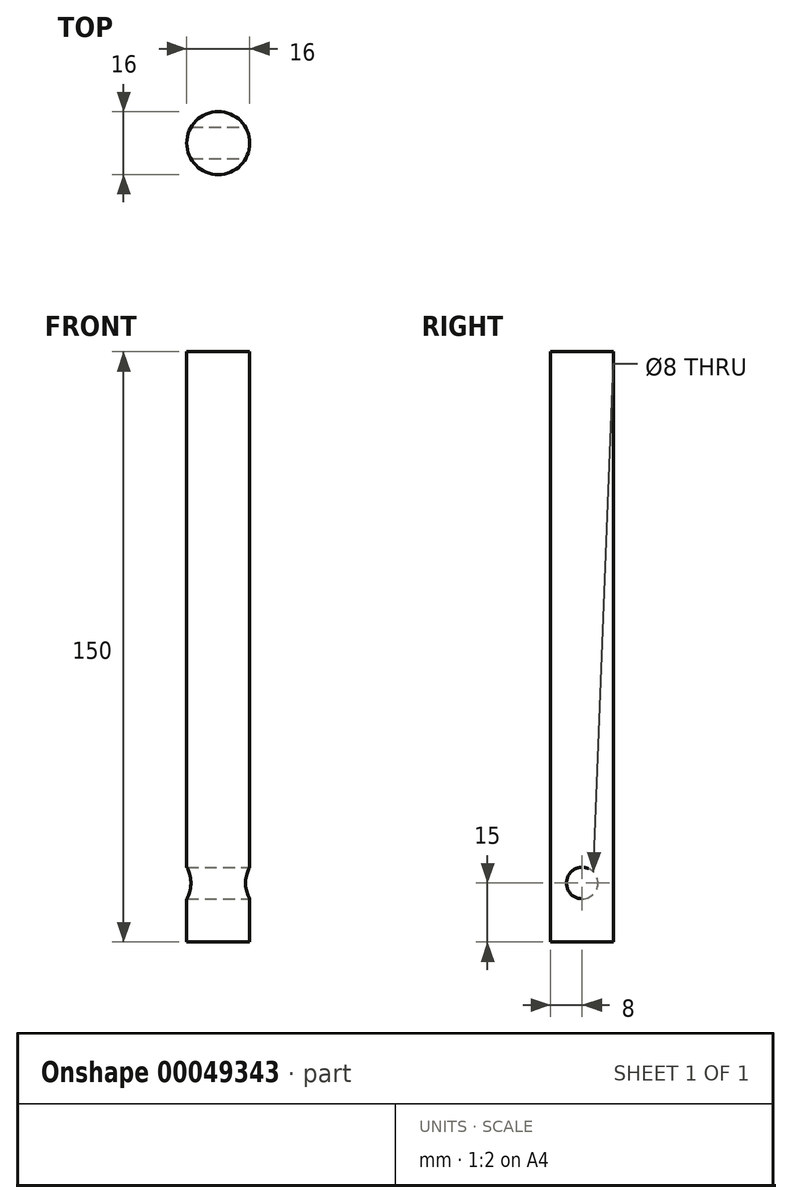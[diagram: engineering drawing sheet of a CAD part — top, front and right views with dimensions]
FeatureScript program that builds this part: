
annotation { "Feature Type Name" : "Feature", "Feature Type Description" : "" }
export const myFeature = defineFeature(function(context is Context, id is Id, definition is map)
    precondition{}
    {
        {
            var Q0;
            Q0=qCreatedBy(makeId("Top.planeOp"),FACE);
            var sketch = newSketch(context, id + "F0", { "sketchPlane" : qUnion([Q0])});
            skCircle(sketch, "E0", {"center": v(0, 0) * mm, "radius": 8 * mm});
            skSolve(sketch);
        }
        {
            var Q0;
            Q0=qSketchRegion(id+"F0",true);
            extrude(context, id + "F1", {"entities" : qUnion([Q0]), "depth" : 150 * mm});
        }
        {
            var Q0;
            Q0=qCreatedBy(makeId("Right.planeOp"),FACE);
            var sketch = newSketch(context, id + "F2", { "sketchPlane" : qUnion([Q0])});
            skCircle(sketch, "E1", {"center": v(0, 15) * mm, "radius": 4 * mm});
            skSolve(sketch);
        }
        {
            var Q0;
            Q0=qSketchRegion(id+"F2",true);
            extrude(context, id + "F3", {"entities" : qUnion([Q0]), "operationType" : NewBodyOperationType.REMOVE, "oppositeDirection" : true, "depth" : 25 * mm, "hasSecondDirection" : true, "secondDirectionOppositeDirection" : false, "secondDirectionDepth" : 25 * mm});
        }
    });
